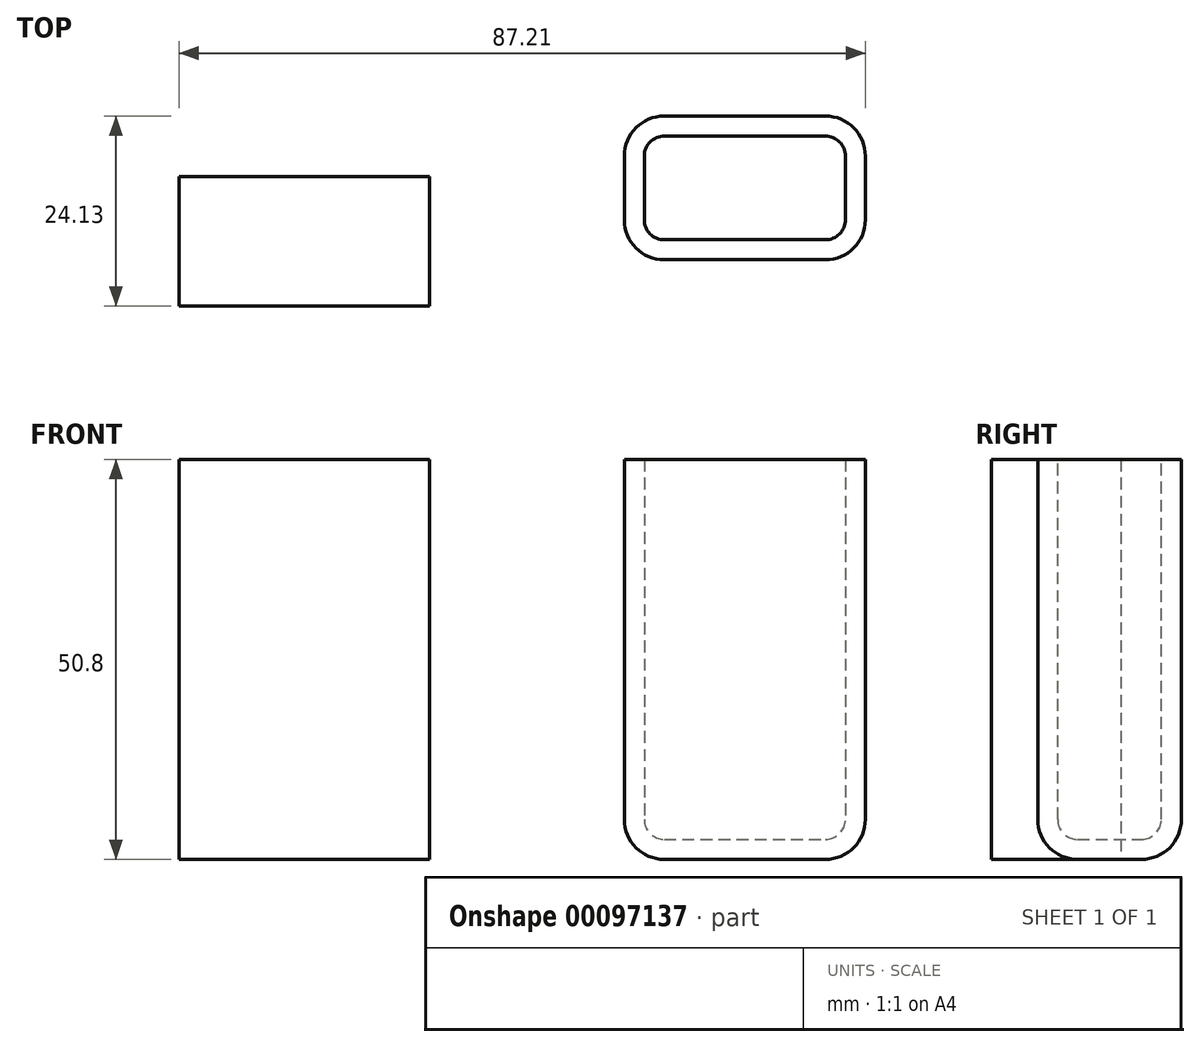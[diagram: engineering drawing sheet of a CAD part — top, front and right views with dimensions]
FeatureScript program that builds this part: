
annotation { "Feature Type Name" : "Feature", "Feature Type Description" : "" }
export const myFeature = defineFeature(function(context is Context, id is Id, definition is map)
    precondition{}
    {
        {
            var Q0;
            Q0=qCreatedBy(makeId("Top.planeOp"),FACE);
            var sketch = newSketch(context, id + "F0", { "sketchPlane" : qUnion([Q0])});
            skLineSegment(sketch, "E0.bottom", {"start": v(-31.23, 33.97) * mm, "end": v(-18.86, 33.97) * mm});
            skLineSegment(sketch, "E0.top", {"start": v(-31.23, 25.86) * mm, "end": v(-18.86, 25.86) * mm});
            skLineSegment(sketch, "E0.left", {"start": v(-31.23, 33.97) * mm, "end": v(-31.23, 25.86) * mm});
            skLineSegment(sketch, "E0.right", {"start": v(-18.86, 33.97) * mm, "end": v(-18.86, 25.86) * mm});
            skLineSegment(sketch, "E1.bottom", {"start": v(-18.86, 24.24) * mm, "end": v(12.98, 24.24) * mm});
            skLineSegment(sketch, "E1.top", {"start": v(-18.86, 7.8) * mm, "end": v(12.98, 7.8) * mm});
            skLineSegment(sketch, "E1.left", {"start": v(-18.86, 24.24) * mm, "end": v(-18.86, 7.8) * mm});
            skLineSegment(sketch, "E1.right", {"start": v(12.98, 24.24) * mm, "end": v(12.98, 7.8) * mm});
            skLineSegment(sketch, "E2.bottom", {"start": v(37.72, 31.94) * mm, "end": v(68.35, 31.94) * mm});
            skLineSegment(sketch, "E2.top", {"start": v(37.72, 13.69) * mm, "end": v(68.35, 13.69) * mm});
            skLineSegment(sketch, "E2.left", {"start": v(37.72, 31.94) * mm, "end": v(37.72, 13.69) * mm});
            skLineSegment(sketch, "E2.right", {"start": v(68.35, 31.94) * mm, "end": v(68.35, 13.69) * mm});
            skSolve(sketch);
        }
        {
            var Q0;
            Q0=makeQuery(id+"F0.imprint","IMPRINT",FACE,{"disambiguationData":[TD([[makeQuery(id+"F0.imprint","IMPRINT",EDGE,{"derivedFrom":sQuery(id+"F0.wireOp",EDGE,"E1.bottom")}),-1.0]])]});
            var Q1;
            Q1=makeQuery(id+"F0.imprint","IMPRINT",FACE,{"disambiguationData":[TD([[makeQuery(id+"F0.imprint","IMPRINT",EDGE,{"derivedFrom":sQuery(id+"F0.wireOp",EDGE,"E2.bottom")}),-1.0]])]});
            extrude(context, id + "F1", {"entities" : qUnion([Q0, Q1]), "depth" : 50.8 * mm});
        }
        {
            var Q0;
            Q0=makeQuery(id+"F1.opExtrude","SWEPT_EDGE",EDGE,{"disambiguationData":[OSD([sQuery(id+"F0.wireOp",EDGE,"E2.top"),sQuery(id+"F0.wireOp",EDGE,"E2.right")])]});
            var Q1;
            Q1=makeQuery(id+"F1.opExtrude","SWEPT_EDGE",EDGE,{"disambiguationData":[OSD([sQuery(id+"F0.wireOp",EDGE,"E2.bottom"),sQuery(id+"F0.wireOp",EDGE,"E2.right")])]});
            var Q2;
            Q2=makeQuery(id+"F1.opExtrude","SWEPT_EDGE",EDGE,{"disambiguationData":[OSD([sQuery(id+"F0.wireOp",EDGE,"E2.top"),sQuery(id+"F0.wireOp",EDGE,"E2.left")])]});
            var Q3;
            Q3=makeQuery(id+"F1.opExtrude","SWEPT_EDGE",EDGE,{"disambiguationData":[OSD([sQuery(id+"F0.wireOp",EDGE,"E2.bottom"),sQuery(id+"F0.wireOp",EDGE,"E2.left")])]});
            fillet(context, id + "F2", {"entities" : qUnion([Q0, Q1, Q2, Q3]), "radius" : 5.08 * mm, "tangentPropagation" : true, "allowEdgeOverflow" : false});
        }
        {
            var Q0;
            Q0=makeQuery(id+"F1.opExtrude","CAP_EDGE",EDGE,{"disambiguationData":[OSD([sQuery(id+"F0.wireOp",EDGE,"E2.bottom")])],"isStart":true});
            fillet(context, id + "F3", {"entities" : qUnion([Q0]), "radius" : 5.08 * mm, "tangentPropagation" : true, "allowEdgeOverflow" : false});
        }
        {
            var Q0;
            Q0=makeQuery(id+"F1.opExtrude","CAP_FACE",FACE,{"disambiguationData":[OSD([sQuery(id+"F0.wireOp",EDGE,"E2.bottom"),sQuery(id+"F0.wireOp",EDGE,"E2.top"),sQuery(id+"F0.wireOp",EDGE,"E2.left"),sQuery(id+"F0.wireOp",EDGE,"E2.right")])],"isStart":false});
            shell(context, id + "F4", {"entities" : qUnion([Q0]), "thickness" : 2.54 * mm});
        }
    });
